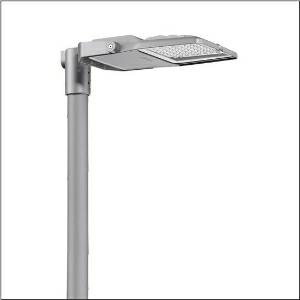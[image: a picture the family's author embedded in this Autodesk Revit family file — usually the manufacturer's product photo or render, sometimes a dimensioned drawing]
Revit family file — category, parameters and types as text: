
# Revit family: floodlight_fl_21_mini___pl33t_5xa7775b2f3a_d5fa
name_source: partatom
category: Lighting Fixtures
units: mm (PartAtom-declared; Revit-internal decimal feet)

## family parameters
Cut with Voids When Loaded = No
Host = Face
Light Source = No
Part Type = Normal
Room Calculation Point = No
Round Connector Dimension = Use Diameter
Shared = No

## types (1)
- --- (1 x LED, 6150 lm, 45.7 W, 3000K)
    Apparent Load = 46 VA
    CIE Flux Codes = 26 75 99 100 100
    Color Rendering = 70
    Color Temperature = 3000K
    Default Elevation = 1800 mm
    Description = Floodlight FL 21 mini, floodlight, primary light control with lens, of PMMA, primary optical cover: protective disc, of toughened safety glass, transparent, light distribution: PL33T, light emission: direct distribution, installation type: surface-mounted, LED, High Power LED, rated luminous flux: 6.150lm, luminous efficacy: 135lm/W, light colour: 730, colour temperature: 3000K, control gear: Smart Interface (Zhaga), control: flexible luminous flux parameterisation, time-dependent luminous flux control, constant luminous flux control, overheat protection, pre-setting: logarithmic dimming characteristic, with terminal, 6-pole, mains connection: 220..240V, AC, 50/60Hz, start of lifetime: 46W, end of service life: 48W, reduction: 22W, luminaire housing, of diecast aluminium, powder-coated, Siteco® metallic grey (DB 702S), corrosivity category C5 mid according to DIN EN ISO 12944, suitable for swimming pools, chlorine-resistant, sealing non-destructively replaceable, please order mast flange separately, mast bracket, of steel, galvanised, powder-coated, Siteco® metallic grey (DB 702S), Smart Interface above, protection rating (complete): IP66, insulation class (complete): insulation class II (safety insulation), certification: CE, ENEC, VDE, protection symbol: D, impact resistance: IK08, permissible operating ambient temperature: -40..+40°C, permissible operating ambient temperature for outdoor applications: -40..+50°C, standard: DIN EN 12944, LABS conformity tested according to VDMA 24364:2018-05, packaging unit: 1 piece

Light Distribution: PL33T
    Height = 70 mm
    Lamp = 1 x LED
    Lamp Light Flux = 6150 lm
    Lamp Power = 45.7 W
    Lamp count = 1
    Length = 485 mm
    Luminous efficacy = 135 lm/W
    Manufacturer = Siteco
    ModVariant = No
    Model = 5XA7775B2F3A
    Number of Poles = 1
    OnlyDefault = Yes
    Power Factor = 1
    Product Name = Floodlight FL 21 mini | PL33T
    Product group = floodlight | pylon annexe
    ProductGroupID = 6200
    Protection Class = Protection class II
    Protection Degree = IP 66
    RLX_Detail_Level = 1
    RLX_Emergency_Light_Flux = 0 lm
    RLX_Emergency_Type = 0
    RLX_Emergency_Type_DB = No
    RlxData = <blob elided: 100889 chars, md5=94c426d5>
    Socket = socket
    Standby Power = 0 W
    System Light Flux = 6150 lm
    System Power = 46 W
    Type Comments = factory setting: luminous flux: 100 % | dim-lin: 254 | 463 mA
    Type Image = l_1007125.jpg
    URL = http://relux.com
    VarID = @adj_148674
    Voltage = 0 V
    Weight = 0.00 kg
    Width = 337 mm

## geometry (parser evidence)
native form markers: Blend x4, Sweep x13
no freeform markers — native parametric forms only
